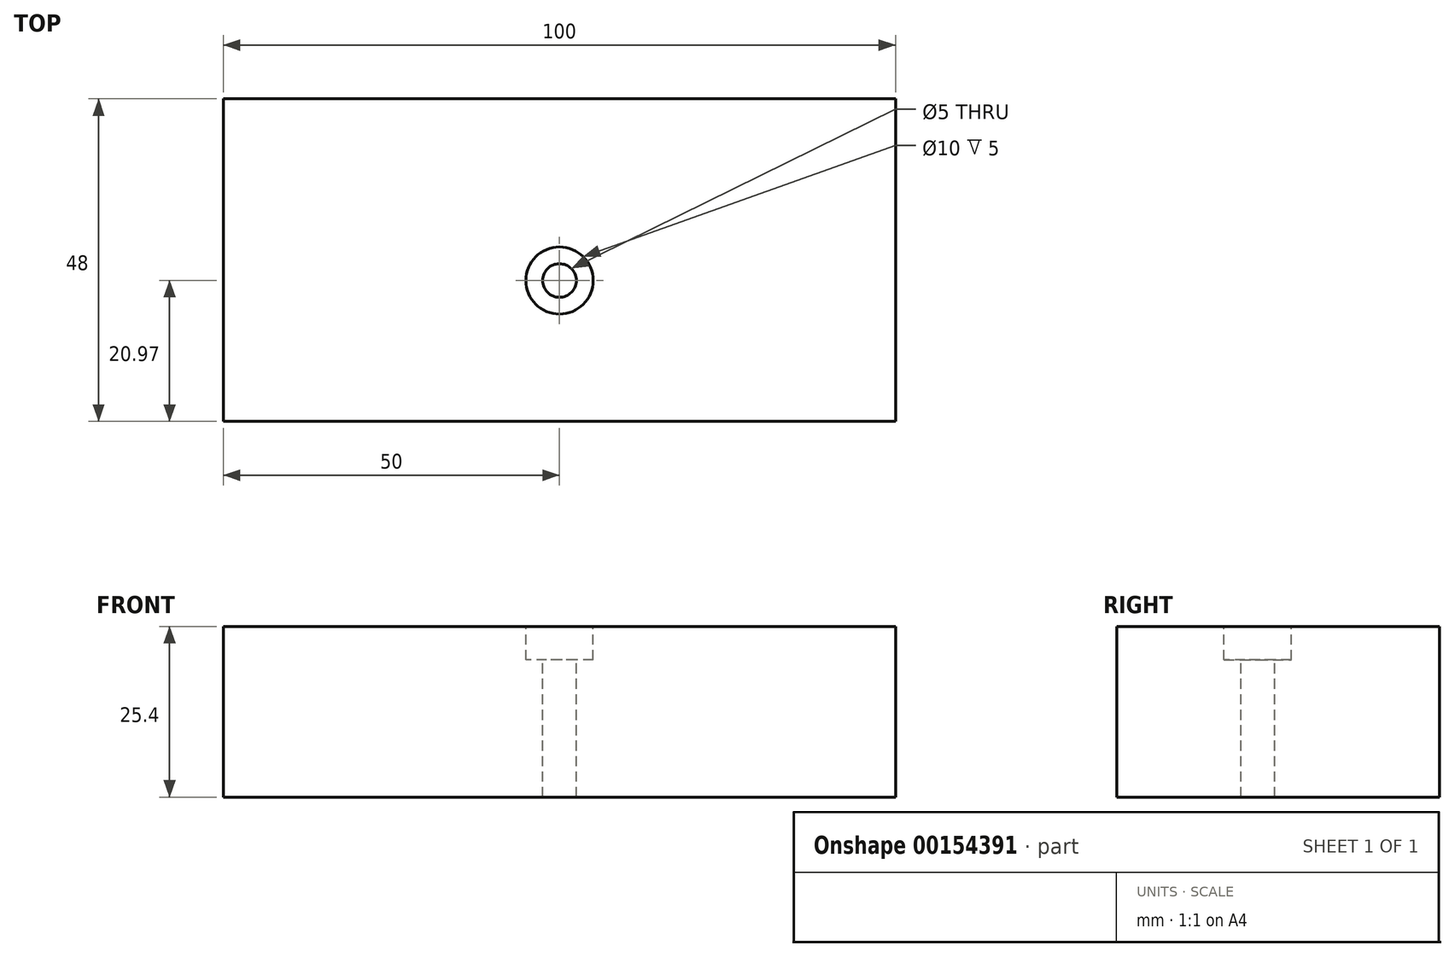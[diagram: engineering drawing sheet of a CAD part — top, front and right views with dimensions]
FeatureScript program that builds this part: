
annotation { "Feature Type Name" : "Feature", "Feature Type Description" : "" }
export const myFeature = defineFeature(function(context is Context, id is Id, definition is map)
    precondition{}
    {
        {
            var Q0;
            Q0=qCreatedBy(makeId("Top.planeOp"),FACE);
            var sketch = newSketch(context, id + "F0", { "sketchPlane" : qUnion([Q0])});
            skLineSegment(sketch, "E0", {"start": v(-50, -20.97) * mm, "end": v(-50, 27.03) * mm});
            skLineSegment(sketch, "E1", {"start": v(-50, 27.03) * mm, "end": v(50, 27.03) * mm});
            skLineSegment(sketch, "E2", {"start": v(-50, -20.97) * mm, "end": v(50, -20.97) * mm});
            skLineSegment(sketch, "E3", {"start": v(50, 27.03) * mm, "end": v(50, -20.97) * mm});
            skSolve(sketch);
        }
        {
            var Q0;
            Q0 = qSketchRegion(id + "F0", true);
            extrude(context, id + "F1", {"entities" : qUnion([Q0]), "depth" : 25.4 * mm});
        }
        {
            var Q0;
            Q0=makeQuery(id+"F1.opExtrude","CAP_FACE",FACE,{"disambiguationData":[OSD([sQuery(id+"F0.wireOp",EDGE,"E0"),sQuery(id+"F0.wireOp",EDGE,"E1"),sQuery(id+"F0.wireOp",EDGE,"E2"),sQuery(id+"F0.wireOp",EDGE,"E3")])],"isStart":false});
            var sketch = newSketch(context, id + "F2", { "sketchPlane" : qUnion([Q0])});
            skPoint(sketch, "E4", {"position": v(0, 0) * mm});
            skSolve(sketch);
        }
        {
            var Q0;
            Q0=sQuery(id+"F2.wireOp",VERTEX,"E4");
            var Q1;
            Q1=makeQuery(id+"F1.opExtrude","SWEPT_BODY",BODY,{"disambiguationData":[OSD([sQuery(id+"F0.wireOp",EDGE,"E0"),sQuery(id+"F0.wireOp",EDGE,"E1"),sQuery(id+"F0.wireOp",EDGE,"E2"),sQuery(id+"F0.wireOp",EDGE,"E3")])]});
            hole(context, id + "F3", {"style" : HoleStyle.C_BORE, "endStyle" : HoleEndStyle.THROUGH, "holeDiameter" : 5 * mm, "cBoreDiameter" : 10 * mm, "cBoreDepth" : 5 * mm, "locations" : qUnion([Q0]), "scope" : qUnion([Q1]), "isTappedThrough" : true});
        }
    });
